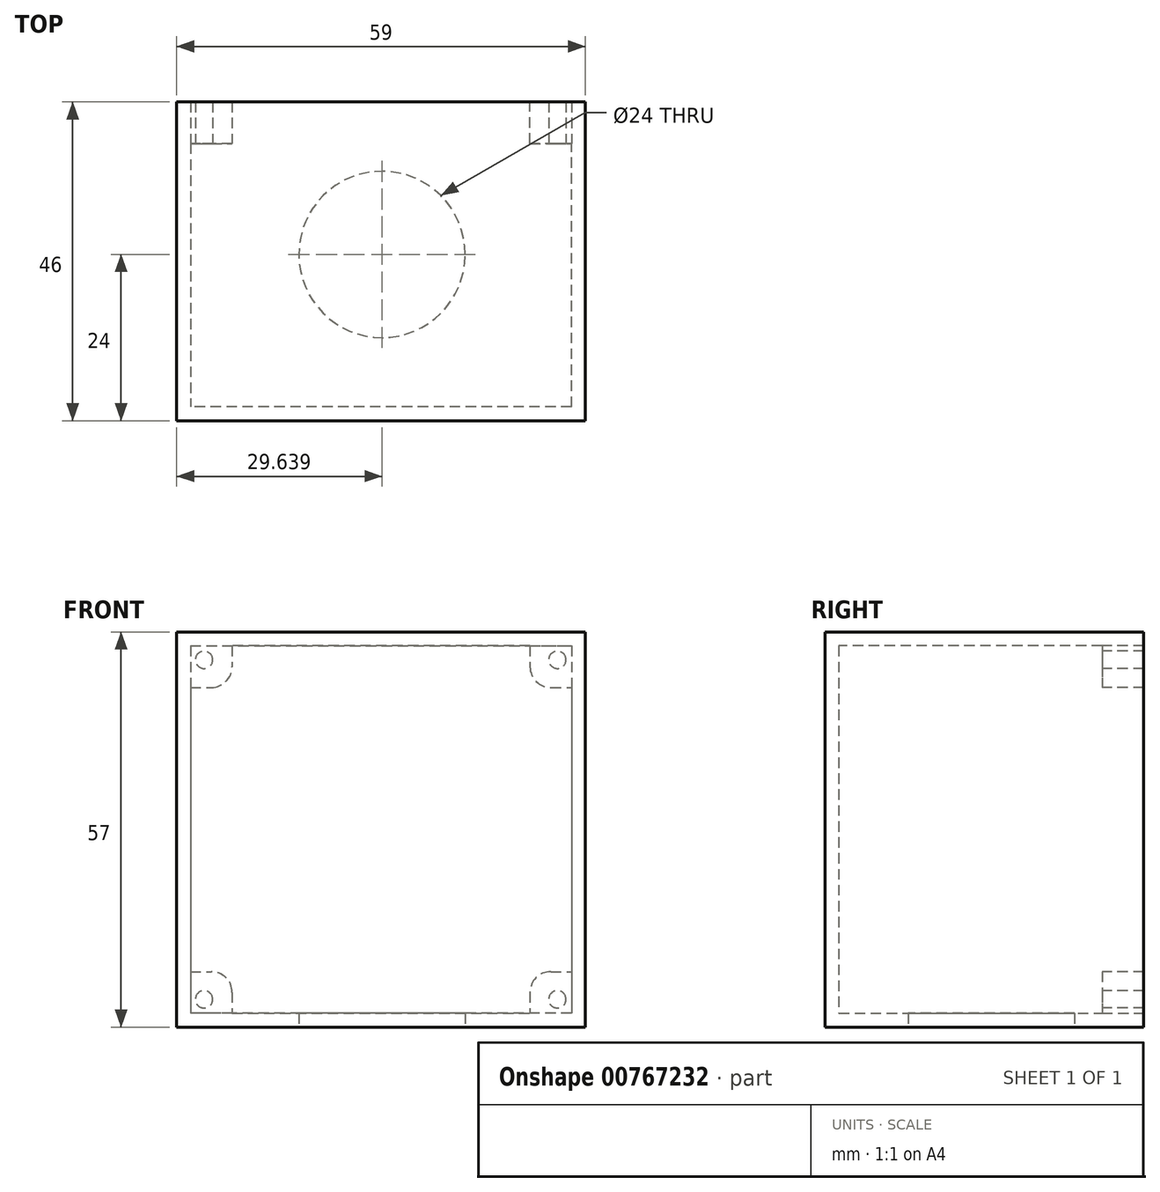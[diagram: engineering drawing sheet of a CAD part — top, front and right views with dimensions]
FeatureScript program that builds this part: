
annotation { "Feature Type Name" : "Feature", "Feature Type Description" : "" }
export const myFeature = defineFeature(function(context is Context, id is Id, definition is map)
    precondition{}
    {
        {
            var Q0;
            Q0=qCreatedBy(makeId("Top.planeOp"),FACE);
            var sketch = newSketch(context, id + "F0", { "sketchPlane" : qUnion([Q0])});
            skLineSegment(sketch, "E0.bottom", {"start": v(-29.62, 46) * mm, "end": v(29.38, 46) * mm});
            skLineSegment(sketch, "E0.top", {"start": v(-29.62, 0) * mm, "end": v(29.38, 0) * mm});
            skLineSegment(sketch, "E0.left", {"start": v(-29.62, 46) * mm, "end": v(-29.62, 0) * mm});
            skLineSegment(sketch, "E0.right", {"start": v(29.38, 46) * mm, "end": v(29.38, 0) * mm});
            skCircle(sketch, "E1", {"center": v(0.02, 24) * mm, "radius": 12 * mm});
            skLineSegment(sketch, "E2.bottom", {"start": v(-27.62, 46) * mm, "end": v(27.38, 46) * mm});
            skLineSegment(sketch, "E2.top", {"start": v(-27.62, 2) * mm, "end": v(27.38, 2) * mm});
            skLineSegment(sketch, "E2.left", {"start": v(-27.62, 46) * mm, "end": v(-27.62, 2) * mm});
            skLineSegment(sketch, "E2.right", {"start": v(27.38, 46) * mm, "end": v(27.38, 2) * mm});
            skLineSegment(sketch, "E3.bottom", {"start": v(-27.62, 40) * mm, "end": v(-21.62, 40) * mm});
            skLineSegment(sketch, "E3.top", {"start": v(-27.62, 46) * mm, "end": v(-21.62, 46) * mm});
            skLineSegment(sketch, "E3.left", {"start": v(-27.62, 40) * mm, "end": v(-27.62, 46) * mm});
            skLineSegment(sketch, "E3.right", {"start": v(-21.62, 40) * mm, "end": v(-21.62, 46) * mm});
            skLineSegment(sketch, "E4.bottom", {"start": v(21.38, 46) * mm, "end": v(27.38, 46) * mm});
            skLineSegment(sketch, "E4.top", {"start": v(21.38, 40) * mm, "end": v(27.38, 40) * mm});
            skLineSegment(sketch, "E4.left", {"start": v(21.38, 46) * mm, "end": v(21.38, 40) * mm});
            skLineSegment(sketch, "E4.right", {"start": v(27.38, 46) * mm, "end": v(27.38, 40) * mm});
            skSolve(sketch);
        }
        {
            var Q0;
            Q0=makeQuery(id+"F0.imprint","IMPRINT",FACE,{"disambiguationData":[TD([[makeQuery(id+"F0.imprint","IMPRINT",EDGE,{"derivedFrom":sQuery(id+"F0.wireOp",EDGE,"E0.top")}),1.0]])]});
            var Q1;
            Q1=makeQuery(id+"F0.imprint","IMPRINT",FACE,{"disambiguationData":[TD([[makeQuery(id+"F0.imprint","IMPRINT",EDGE,{"derivedFrom":sQuery(id+"F0.wireOp",EDGE,"E1")}),-1.0]])]});
            var Q2;
            {var subQ4=sQuery(id+"F0.wireOp",EDGE,"E3.bottom");Q2=makeQuery(id+"F0.imprint","IMPRINT",FACE,{"disambiguationData":[TD([[makeQuery(id+"F0.imprint","IMPRINT",EDGE,{"derivedFrom":subQ4}),1.0]])]});}
            var Q3;
            {var subQ4=sQuery(id+"F0.wireOp",EDGE,"E4.top");Q3=makeQuery(id+"F0.imprint","IMPRINT",FACE,{"disambiguationData":[TD([[makeQuery(id+"F0.imprint","IMPRINT",EDGE,{"derivedFrom":subQ4}),1.0]])]});}
            extrude(context, id + "F1", {"entities" : qUnion([Q0, Q1, Q2, Q3]), "depth" : 2 * mm, "offsetDistance" : 25 * mm});
        }
        {
            var Q0;
            Q0=makeQuery(id+"F0.imprint","IMPRINT",FACE,{"disambiguationData":[TD([[makeQuery(id+"F0.imprint","IMPRINT",EDGE,{"derivedFrom":sQuery(id+"F0.wireOp",EDGE,"E0.top")}),1.0]])]});
            extrude(context, id + "F2", {"entities" : qUnion([Q0]), "operationType" : NewBodyOperationType.ADD, "depth" : 57 * mm, "offsetDistance" : 25 * mm});
        }
        {
            var Q0;
            Q0=qCreatedBy(makeId("Front.planeOp"),FACE);
            var sketch = newSketch(context, id + "F3", { "sketchPlane" : qUnion([Q0])});
            skLineSegment(sketch, "E5.bottom", {"start": v(27.38, 57) * mm, "end": v(-27.62, 57) * mm});
            skLineSegment(sketch, "E5.top", {"start": v(27.38, 55) * mm, "end": v(-27.62, 55) * mm});
            skLineSegment(sketch, "E5.left", {"start": v(27.38, 57) * mm, "end": v(27.38, 55) * mm});
            skLineSegment(sketch, "E5.right", {"start": v(-27.62, 57) * mm, "end": v(-27.62, 55) * mm});
            skSolve(sketch);
        }
        {
            var Q0;
            Q0=makeQuery(id+"F3.imprint","IMPRINT",FACE,{"disambiguationData":[TD([[makeQuery(id+"F3.imprint","IMPRINT",EDGE,{"derivedFrom":sQuery(id+"F3.wireOp",EDGE,"E5.bottom")}),1.0]])]});
            extrude(context, id + "F4", {"entities" : qUnion([Q0]), "operationType" : NewBodyOperationType.ADD, "oppositeDirection" : true, "depth" : 46 * mm, "offsetDistance" : 25 * mm});
        }
        {
            var Q0;
            {var subQ4=sQuery(id+"F0.wireOp",EDGE,"E4.top");Q0=makeQuery(id+"F0.imprint","IMPRINT",FACE,{"disambiguationData":[TD([[makeQuery(id+"F0.imprint","IMPRINT",EDGE,{"derivedFrom":subQ4}),1.0]])]});}
            var Q1;
            {var subQ4=sQuery(id+"F0.wireOp",EDGE,"E3.bottom");Q1=makeQuery(id+"F0.imprint","IMPRINT",FACE,{"disambiguationData":[TD([[makeQuery(id+"F0.imprint","IMPRINT",EDGE,{"derivedFrom":subQ4}),1.0]])]});}
            extrude(context, id + "F5", {"entities" : qUnion([Q0, Q1]), "operationType" : NewBodyOperationType.ADD, "depth" : 8 * mm, "offsetDistance" : 25 * mm});
        }
        {
            var Q0;
            {var subQ4=sQuery(id+"F0.wireOp",EDGE,"E4.top");Q0=makeQuery(id+"F0.imprint","IMPRINT",FACE,{"disambiguationData":[TD([[makeQuery(id+"F0.imprint","IMPRINT",EDGE,{"derivedFrom":subQ4}),1.0]])]});}
            var Q1;
            {var subQ4=sQuery(id+"F0.wireOp",EDGE,"E3.bottom");Q1=makeQuery(id+"F0.imprint","IMPRINT",FACE,{"disambiguationData":[TD([[makeQuery(id+"F0.imprint","IMPRINT",EDGE,{"derivedFrom":subQ4}),1.0]])]});}
            extrude(context, id + "F6", {"entities" : qUnion([Q0, Q1]), "operationType" : NewBodyOperationType.ADD, "depth" : 55 * mm, "offsetDistance" : 25 * mm, "hasSecondDirection" : true, "secondDirectionOppositeDirection" : false, "secondDirectionDepth" : 49 * mm});
        }
        {
            var Q0;
            Q0=qCreatedBy(makeId("Front.planeOp"),FACE);
            var sketch = newSketch(context, id + "F7", { "sketchPlane" : qUnion([Q0])});
            skLineSegment(sketch, "E6.bottom", {"start": v(29.33, 57) * mm, "end": v(-29.67, 57) * mm});
            skLineSegment(sketch, "E6.top", {"start": v(29.33, 0) * mm, "end": v(-29.67, 0) * mm});
            skLineSegment(sketch, "E6.left", {"start": v(29.33, 57) * mm, "end": v(29.33, 0) * mm});
            skLineSegment(sketch, "E6.right", {"start": v(-29.67, 57) * mm, "end": v(-29.67, 0) * mm});
            skCircle(sketch, "E7", {"center": v(25.33, 53) * mm, "radius": 1.25 * mm});
            skCircle(sketch, "E8", {"center": v(-25.67, 53) * mm, "radius": 1.25 * mm});
            skCircle(sketch, "E9", {"center": v(25.33, 4) * mm, "radius": 1.25 * mm});
            skCircle(sketch, "E10", {"center": v(-25.67, 4) * mm, "radius": 1.25 * mm});
            skSolve(sketch);
        }
        {
            var Q0;
            Q0=makeQuery(id+"F7.imprint","IMPRINT",FACE,{"disambiguationData":[TD([[makeQuery(id+"F7.imprint","IMPRINT",EDGE,{"derivedFrom":sQuery(id+"F7.wireOp",EDGE,"E7")}),1.0]])]});
            var Q1;
            Q1=makeQuery(id+"F7.imprint","IMPRINT",FACE,{"disambiguationData":[TD([[makeQuery(id+"F7.imprint","IMPRINT",EDGE,{"derivedFrom":sQuery(id+"F7.wireOp",EDGE,"E8")}),1.0]])]});
            var Q2;
            Q2=makeQuery(id+"F7.imprint","IMPRINT",FACE,{"disambiguationData":[TD([[makeQuery(id+"F7.imprint","IMPRINT",EDGE,{"derivedFrom":sQuery(id+"F7.wireOp",EDGE,"E10")}),1.0]])]});
            var Q3;
            Q3=makeQuery(id+"F7.imprint","IMPRINT",FACE,{"disambiguationData":[TD([[makeQuery(id+"F7.imprint","IMPRINT",EDGE,{"derivedFrom":sQuery(id+"F7.wireOp",EDGE,"E9")}),1.0]])]});
            extrude(context, id + "F8", {"entities" : qUnion([Q0, Q1, Q2, Q3]), "operationType" : NewBodyOperationType.REMOVE, "oppositeDirection" : true, "depth" : 59 * mm, "offsetDistance" : 25 * mm, "hasSecondDirection" : true, "secondDirectionOppositeDirection" : true, "secondDirectionDepth" : 28.2 * mm});
        }
        {
            var Q0;
            Q0=makeQuery(id+"F6.opExtrude","CAP_EDGE",EDGE,{"disambiguationData":[OSD([sQuery(id+"F0.wireOp",EDGE,"E4.left")])],"isStart":true});
            var Q1;
            Q1=makeQuery(id+"F6.opExtrude","CAP_EDGE",EDGE,{"disambiguationData":[OSD([sQuery(id+"F0.wireOp",EDGE,"E3.right")])],"isStart":true});
            var Q2;
            Q2=makeQuery(id+"F5.opExtrude","CAP_EDGE",EDGE,{"disambiguationData":[OSD([sQuery(id+"F0.wireOp",EDGE,"E3.right")])],"isStart":false});
            var Q3;
            Q3=makeQuery(id+"F5.opExtrude","CAP_EDGE",EDGE,{"disambiguationData":[OSD([sQuery(id+"F0.wireOp",EDGE,"E4.left")])],"isStart":false});
            fillet(context, id + "F9", {"entities" : qUnion([Q0, Q1, Q2, Q3]), "radius" : 3 * mm, "tangentPropagation" : true, "allowEdgeOverflow" : false});
        }
    });
